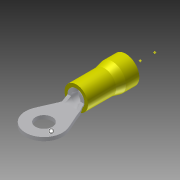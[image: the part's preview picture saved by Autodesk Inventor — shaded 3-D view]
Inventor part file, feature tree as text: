
AUTODESK INVENTOR PART (.ipt)
format: ipt  version: 2011 (Build 150239000, 239)  size: 176,640 bytes
history: native  units: mm
features: other x4, plane x2, imported_body x1, sketch x1
ambient origin geometry x8: Origin, YZ Plane, XZ Plane, XY Plane, X Axis, Y Axis, Z Axis, Center Point
bodies: Solid1 (feature_tree)
feature tree (8):
  imported_body  "Base1"
  sketch  "Sketch1"  dims[d0=3.175mm d1=6.35mm d2=0.0mm]
  other  "Work Point2"
  other  "Work Point3"
  plane  "Work Plane1"
  other  "Work Axis1"
  plane  "Work Plane2"
  other  "Work Axis2"
